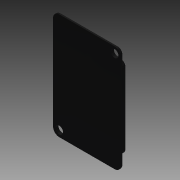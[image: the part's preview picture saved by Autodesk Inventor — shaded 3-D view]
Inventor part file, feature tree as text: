
AUTODESK INVENTOR PART (.ipt)
format: ipt  version: 2013 (Build 170138000, 138)  size: 158,720 bytes
history: native  units: in
note: dims shown in document units (in); Inventor stores cm internally (conversion verified against a paired STEP export)
features: extrude x2, chamfer x2, sketch x2
ambient origin geometry x8: Origin, YZ Plane, XZ Plane, XY Plane, X Axis, Y Axis, Z Axis, Center Point
bodies: Solid1 (feature_tree)
feature tree (6):
  extrude  "Extrusion1"  Depth=0.8661in
  extrude  "Extrusion2"  Depth=0.0394in TaperAngle=0.0deg
  chamfer  "Chamfer1"  Distance=0.0787in
  chamfer  "Chamfer2"  Distance=0.1575in
  sketch  "Sketch1"  dims[d0=0.0787in d1=0.8661in]
  sketch  "Sketch2"  dims[d2=1.0433in d3=0.0394in d4=0.0in d5=0.0787in d6=0.1575in d7=0.1575in d8=0.0984in d9=0.0984in d10=0.0394in d11=0.0in d12=0.0197in d13=0.0787in d14=45.0deg d15=0.0197in d16=0.0787in d17=45.0deg d18=1.3583in d19=1.0433in d20=0.8661in]
